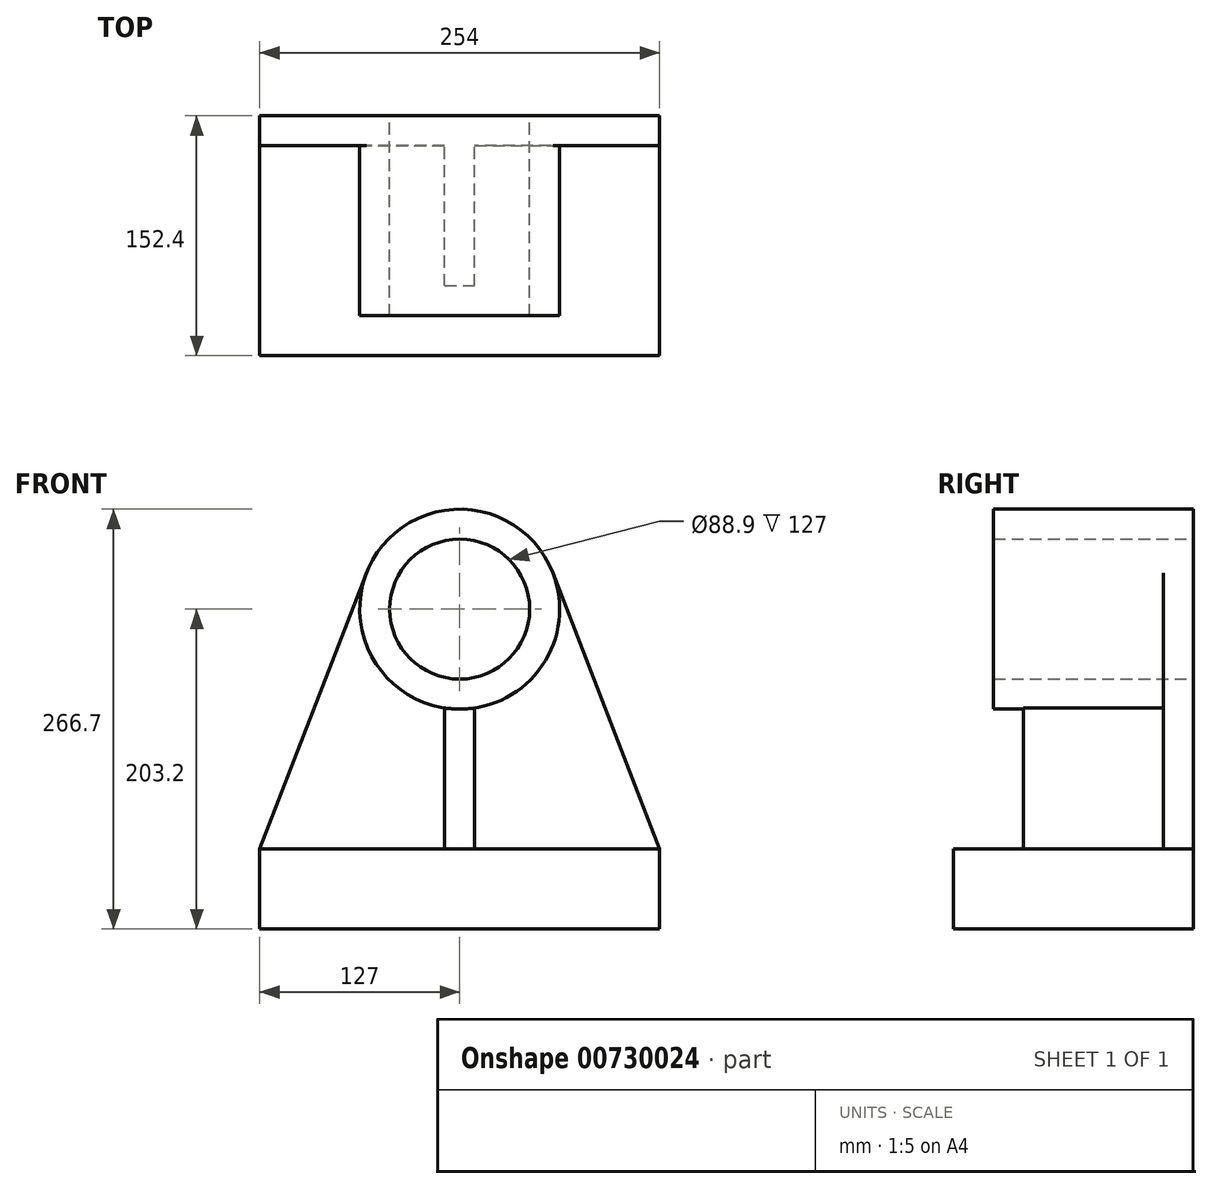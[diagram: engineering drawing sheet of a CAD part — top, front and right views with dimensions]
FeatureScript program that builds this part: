
annotation { "Feature Type Name" : "Feature", "Feature Type Description" : "" }
export const myFeature = defineFeature(function(context is Context, id is Id, definition is map)
    precondition{}
    {
        {
            var Q0;
            Q0=qCreatedBy(makeId("Front.planeOp"),FACE);
            var sketch = newSketch(context, id + "F0", { "sketchPlane" : qUnion([Q0])});
            skArc(sketch, "E0", {"start": v(59.23, 226.1) * mm, "mid": v(0, 266.7) * mm, "end": v(-59.23, 226.1) * mm});
            skCircle(sketch, "E1", {"center": v(0, 203.2) * mm, "radius": 44.45 * mm});
            skLineSegment(sketch, "E2", {"start": v(-59.23, 226.1) * mm, "end": v(-127, 50.8) * mm});
            skLineSegment(sketch, "E3", {"start": v(-127, 50.8) * mm, "end": v(-127, 0) * mm});
            skLineSegment(sketch, "E4", {"start": v(-127, 0) * mm, "end": v(127, 0) * mm});
            skLineSegment(sketch, "E5", {"start": v(127, 0) * mm, "end": v(127, 50.8) * mm});
            skLineSegment(sketch, "E6", {"start": v(127, 50.8) * mm, "end": v(59.23, 226.1) * mm});
            skSolve(sketch);
        }
        {
            var Q0;
            Q0=makeQuery(id+"F0.imprint","IMPRINT",FACE,{"disambiguationData":[TD([[makeQuery(id+"F0.imprint","IMPRINT",EDGE,{"derivedFrom":sQuery(id+"F0.wireOp",EDGE,"E0")}),1.0]])]});
            extrude(context, id + "F1", {"entities" : qUnion([Q0]), "depth" : 19.05 * mm, "offsetDistance" : 25.4 * mm});
        }
        {
            var Q0;
            Q0=qCreatedBy(makeId("Front.planeOp"),FACE);
            var sketch = newSketch(context, id + "F2", { "sketchPlane" : qUnion([Q0])});
            skCircle(sketch, "E7.0", {"center": v(0, 203.2) * mm, "radius": 44.45 * mm});
            skArc(sketch, "E8.0", {"start": v(59.23, 226.1) * mm, "mid": v(0, 266.7) * mm, "end": v(-59.23, 226.1) * mm});
            skArc(sketch, "E9.converted", {"start": v(9.52, 140.42) * mm, "mid": v(0, 266.7) * mm, "end": v(-9.53, 140.42) * mm});
            skPoint(sketch, "E10.orphan", {"position": v(-59.23, 226.1) * mm});
            skLineSegment(sketch, "E11", {"start": v(-9.53, 140.42) * mm, "end": v(-9.53, 50.8) * mm});
            skLineSegment(sketch, "E12", {"start": v(-9.53, 50.8) * mm, "end": v(0, 50.8) * mm});
            skLineSegment(sketch, "E13", {"start": v(0, 50.8) * mm, "end": v(0, 139.7) * mm, "construction": true});
            skLineSegment(sketch, "E14.MirrorCS", {"start": v(9.52, 140.42) * mm, "end": v(9.52, 50.8) * mm});
            skLineSegment(sketch, "E15.MirrorCS", {"start": v(9.52, 50.8) * mm, "end": v(0, 50.8) * mm});
            skSolve(sketch);
        }
        {
            var Q0;
            Q0 = qSketchRegion(id + "F2", true);
            extrude(context, id + "F3", {"entities" : qUnion([Q0]), "operationType" : NewBodyOperationType.ADD, "depth" : 127 * mm, "offsetDistance" : 25.4 * mm});
        }
        {
            var Q0;
            Q0=qCreatedBy(makeId("Front.planeOp"),FACE);
            var sketch = newSketch(context, id + "F4", { "sketchPlane" : qUnion([Q0])});
            skLineSegment(sketch, "E16.0", {"start": v(-127, 0) * mm, "end": v(127, 0) * mm});
            skLineSegment(sketch, "E17.0", {"start": v(-127, 50.8) * mm, "end": v(-127, 0) * mm});
            skLineSegment(sketch, "E18.0", {"start": v(127, 0) * mm, "end": v(127, 50.8) * mm});
            skLineSegment(sketch, "E19", {"start": v(-127, 50.8) * mm, "end": v(127, 50.8) * mm});
            skSolve(sketch);
        }
        {
            var Q0;
            Q0 = qSketchRegion(id + "F4", true);
            extrude(context, id + "F5", {"entities" : qUnion([Q0]), "operationType" : NewBodyOperationType.ADD, "depth" : 152.4 * mm, "offsetDistance" : 25.4 * mm});
        }
        {
            var Q0;
            Q0=makeQuery(id+"F3.opExtrude","CAP_FACE",FACE,{"disambiguationData":[OSD([sQuery(id+"F2.wireOp",EDGE,"E7.0"),sQuery(id+"F2.wireOp",EDGE,"E9.converted"),sQuery(id+"F2.wireOp",EDGE,"E11"),sQuery(id+"F2.wireOp",EDGE,"E12"),sQuery(id+"F2.wireOp",EDGE,"E14.MirrorCS"),sQuery(id+"F2.wireOp",EDGE,"E15.MirrorCS")])],"isStart":false});
            var sketch = newSketch(context, id + "F6", { "sketchPlane" : qUnion([Q0])});
            skLineSegment(sketch, "E20.0", {"start": v(9.52, 140.42) * mm, "end": v(9.52, 50.8) * mm});
            skLineSegment(sketch, "E21.0", {"start": v(-9.53, 140.42) * mm, "end": v(-9.53, 50.8) * mm});
            skLineSegment(sketch, "E22.0", {"start": v(-127, 50.8) * mm, "end": v(127, 50.8) * mm});
            skArc(sketch, "E23.converted", {"start": v(-9.53, 140.42) * mm, "mid": v(0, 139.7) * mm, "end": v(9.52, 140.42) * mm});
            skLineSegment(sketch, "E24", {"start": v(-9.53, 50.8) * mm, "end": v(9.52, 50.8) * mm});
            skSolve(sketch);
        }
        {
            var Q0;
            Q0 = qSketchRegion(id + "F6", true);
            extrude(context, id + "F7", {"entities" : qUnion([Q0]), "operationType" : NewBodyOperationType.REMOVE, "oppositeDirection" : true, "depth" : 19.05 * mm, "offsetDistance" : 25.4 * mm});
        }
    });
